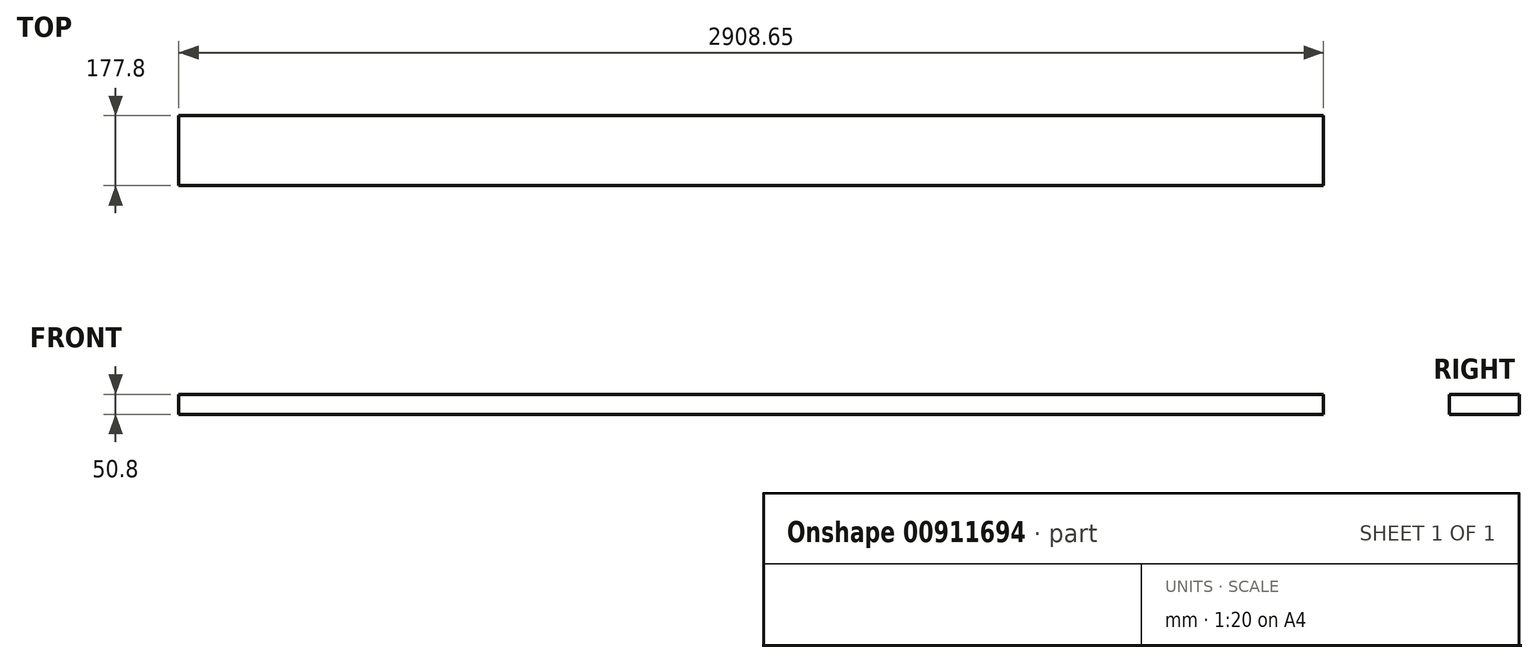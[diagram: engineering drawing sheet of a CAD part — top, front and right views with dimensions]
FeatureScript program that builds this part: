
annotation { "Feature Type Name" : "Feature", "Feature Type Description" : "" }
export const myFeature = defineFeature(function(context is Context, id is Id, definition is map)
    precondition{}
    {
        {
            var Q0;
            Q0=qCreatedBy(makeId("Top.planeOp"),FACE);
            var sketch = newSketch(context, id + "F0", { "sketchPlane" : qUnion([Q0])});
            skLineSegment(sketch, "E0.bottom", {"start": v(-177.48, -177.8) * mm, "end": v(2731.17, -177.8) * mm});
            skLineSegment(sketch, "E0.top", {"start": v(-177.48, 0) * mm, "end": v(2731.17, 0) * mm});
            skLineSegment(sketch, "E0.left", {"start": v(-177.48, -177.8) * mm, "end": v(-177.48, 0) * mm});
            skLineSegment(sketch, "E0.right", {"start": v(2731.17, -177.8) * mm, "end": v(2731.17, 0) * mm});
            skText(sketch, "E1", { "text": "11H", "fontName": "OpenSans-Bold.ttf"});
            const initialGuessF0  = {"E1": [-0.05048, 0, 1, 0, 1.016]};
            skSetInitialGuess(sketch, initialGuessF0);
            skSolve(sketch);
        }
        {
            var Q0;
            {var subQ0=sQuery(id+"F0.wireOp",EDGE,"d5d90416-0cdc-48ac-b64b-d5d0caaf983f.sketch_text.stroke-12");var subQ1=sQuery(id+"F0.wireOp",EDGE,"E0.top");var subQ2=makeQuery(id+"F0.imprint","INTERSECT",VERTEX,{"derivedFrom":[subQ1,subQ0]});Q0=makeQuery(id+"F0.imprint","IMPRINT",FACE,{"disambiguationData":[TD([[makeQuery(id+"F0.imprint","IMPRINT",EDGE,{"disambiguationData":[TD([[subQ2,-1.0]])],"derivedFrom":subQ1}),-1.0]])]});}
            var Q1;
            {var subQ6=sQuery(id+"F0.wireOp",EDGE,"d5d90416-0cdc-48ac-b64b-d5d0caaf983f.sketch_text.stroke-10");Q1=makeQuery(id+"F0.imprint","IMPRINT",FACE,{"disambiguationData":[TD([[makeQuery(id+"F0.imprint","IMPRINT",EDGE,{"derivedFrom":subQ6}),-1.0]])]});}
            var Q2;
            Q2=makeQuery(id+"F0.imprint","IMPRINT",FACE,{"disambiguationData":[TD([[makeQuery(id+"F0.imprint","IMPRINT",EDGE,{"derivedFrom":sQuery(id+"F0.wireOp",EDGE,"E0.bottom")}),1.0]])]});
            var Q3;
            Q3=makeQuery(id+"F0.imprint","IMPRINT",FACE,{"disambiguationData":[TD([[makeQuery(id+"F0.imprint","IMPRINT",EDGE,{"derivedFrom":sQuery(id+"F0.wireOp",EDGE,"d5d90416-0cdc-48ac-b64b-d5d0caaf983f.sketch_text.stroke-26")}),-1.0]])]});
            var Q4;
            Q4=makeQuery(id+"F0.imprint","IMPRINT",FACE,{"disambiguationData":[TD([[makeQuery(id+"F0.imprint","IMPRINT",EDGE,{"derivedFrom":sQuery(id+"F0.wireOp",EDGE,"d5d90416-0cdc-48ac-b64b-d5d0caaf983f.sketch_text.stroke-0")}),-1.0]])]});
            var Q5;
            Q5=makeQuery(id+"F0.imprint","IMPRINT",FACE,{"disambiguationData":[TD([[makeQuery(id+"F0.imprint","IMPRINT",EDGE,{"derivedFrom":sQuery(id+"F0.wireOp",EDGE,"E1.sketch_text.stroke-10")}),-1.0]])]});
            var Q6;
            Q6=makeQuery(id+"F0.imprint","IMPRINT",FACE,{"disambiguationData":[TD([[makeQuery(id+"F0.imprint","IMPRINT",EDGE,{"derivedFrom":sQuery(id+"F0.wireOp",EDGE,"E1.sketch_text.stroke-0")}),-1.0]])]});
            var Q7;
            Q7=makeQuery(id+"F0.imprint","IMPRINT",FACE,{"disambiguationData":[TD([[makeQuery(id+"F0.imprint","IMPRINT",EDGE,{"derivedFrom":sQuery(id+"F0.wireOp",EDGE,"E1.sketch_text.stroke-20")}),-1.0]])]});
            extrude(context, id + "F1", {"entities" : qUnion([Q0, Q1, Q2, Q3, Q4, Q5, Q6, Q7]), "depth" : 50.8 * mm, "offsetDistance" : 25.4 * mm});
        }
    });
